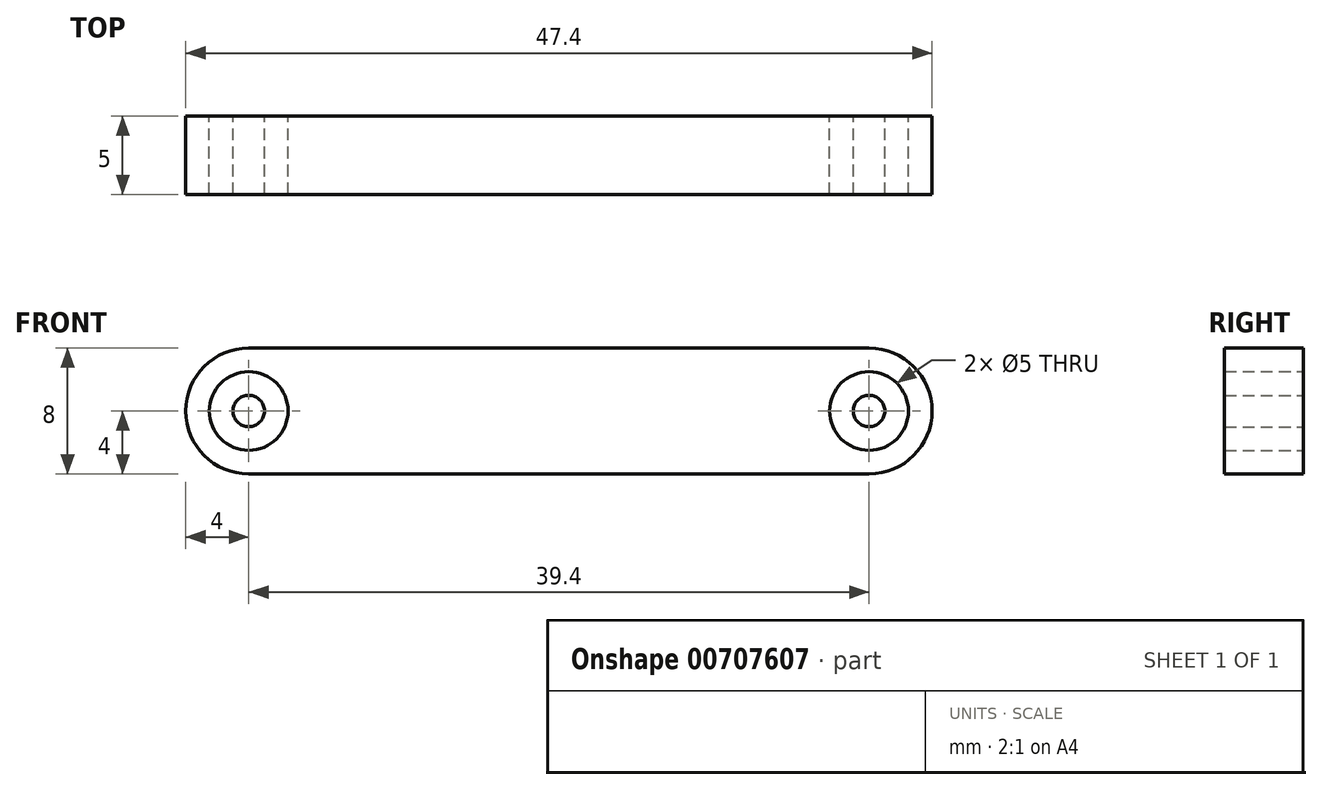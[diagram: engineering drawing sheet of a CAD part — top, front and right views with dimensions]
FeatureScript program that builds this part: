
annotation { "Feature Type Name" : "Feature", "Feature Type Description" : "" }
export const myFeature = defineFeature(function(context is Context, id is Id, definition is map)
    precondition{}
    {
        {
            var Q0;
            Q0=qCreatedBy(makeId("Front.planeOp"),FACE);
            var sketch = newSketch(context, id + "F0", { "sketchPlane" : qUnion([Q0])});
            skArc(sketch, "E0", {"start": v(0, 4) * mm, "mid": v(-4, 0) * mm, "end": v(0, -4) * mm});
            skCircle(sketch, "E1", {"center": v(0, 0) * mm, "radius": 2.5 * mm});
            skCircle(sketch, "E2", {"center": v(0, 0) * mm, "radius": 1 * mm});
            skLineSegment(sketch, "E3", {"start": v(0, 0) * mm, "end": v(39.4, 0) * mm});
            skArc(sketch, "E4", {"start": v(39.4, -4) * mm, "mid": v(43.4, 0) * mm, "end": v(39.4, 4) * mm});
            skCircle(sketch, "E5", {"center": v(39.4, 0) * mm, "radius": 2.5 * mm});
            skCircle(sketch, "E6", {"center": v(39.4, 0) * mm, "radius": 1 * mm});
            skLineSegment(sketch, "E7", {"start": v(0, -4) * mm, "end": v(39.4, -4) * mm});
            skLineSegment(sketch, "E8", {"start": v(0, 4) * mm, "end": v(39.4, 4) * mm});
            skSolve(sketch);
        }
        {
            var Q0;
            Q0=makeQuery(id+"F0.imprint","IMPRINT",FACE,{"disambiguationData":[TD([[makeQuery(id+"F0.imprint","IMPRINT",EDGE,{"derivedFrom":sQuery(id+"F0.wireOp",EDGE,"E2")}),1.0]])]});
            var Q1;
            Q1=makeQuery(id+"F0.imprint","IMPRINT",FACE,{"disambiguationData":[TD([[makeQuery(id+"F0.imprint","IMPRINT",EDGE,{"derivedFrom":sQuery(id+"F0.wireOp",EDGE,"E0")}),1.0]])]});
            var Q2;
            Q2=makeQuery(id+"F0.imprint","IMPRINT",FACE,{"disambiguationData":[TD([[makeQuery(id+"F0.imprint","IMPRINT",EDGE,{"derivedFrom":sQuery(id+"F0.wireOp",EDGE,"E6")}),1.0]])]});
            extrude(context, id + "F1", {"entities" : qUnion([Q0, Q1, Q2]), "depth" : 5 * mm, "offsetDistance" : 25.4 * mm});
        }
    });
